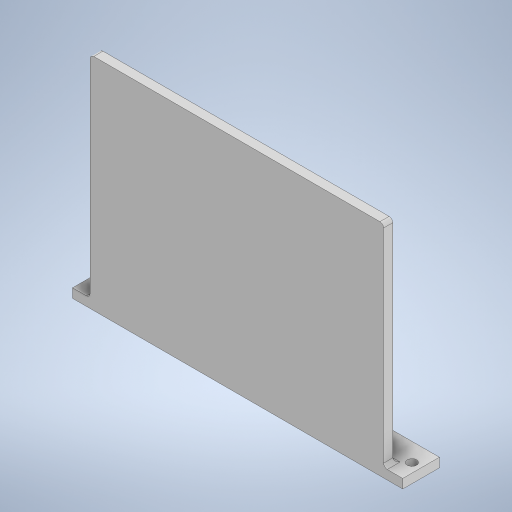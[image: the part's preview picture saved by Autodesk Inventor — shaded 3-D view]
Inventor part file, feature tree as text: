
AUTODESK INVENTOR PART (.ipt)
format: ipt  version: 2024 (Build 280153000, 153)  size: 222,720 bytes
history: native  units: mm
features: sketch x3, extrude x2, other x1, hole x1, fillet x1
ambient origin geometry x8: Origin, YZ Plane, XZ Plane, XY Plane, X Axis, Y Axis, Z Axis, Center Point
bodies: Body1 (feature_tree)
feature tree (8):
  other  "ソリッド1"
  extrude  "押し出し1"  Depth=160.0mm
  extrude  "押し出し2"  Depth=120.0mm
  hole  "穴1"  [1 undecoded]
  fillet  "フィレット1"  Radius=180.0mm
  sketch  "スケッチ1"
  sketch  "スケッチ2"
  sketch  "スケッチ3"
note: 1 required parameter value undecoded (feature->parameter linkage not recoverable at this tier; creation-order binding heuristic only, values carry confidence <= 0.55)
